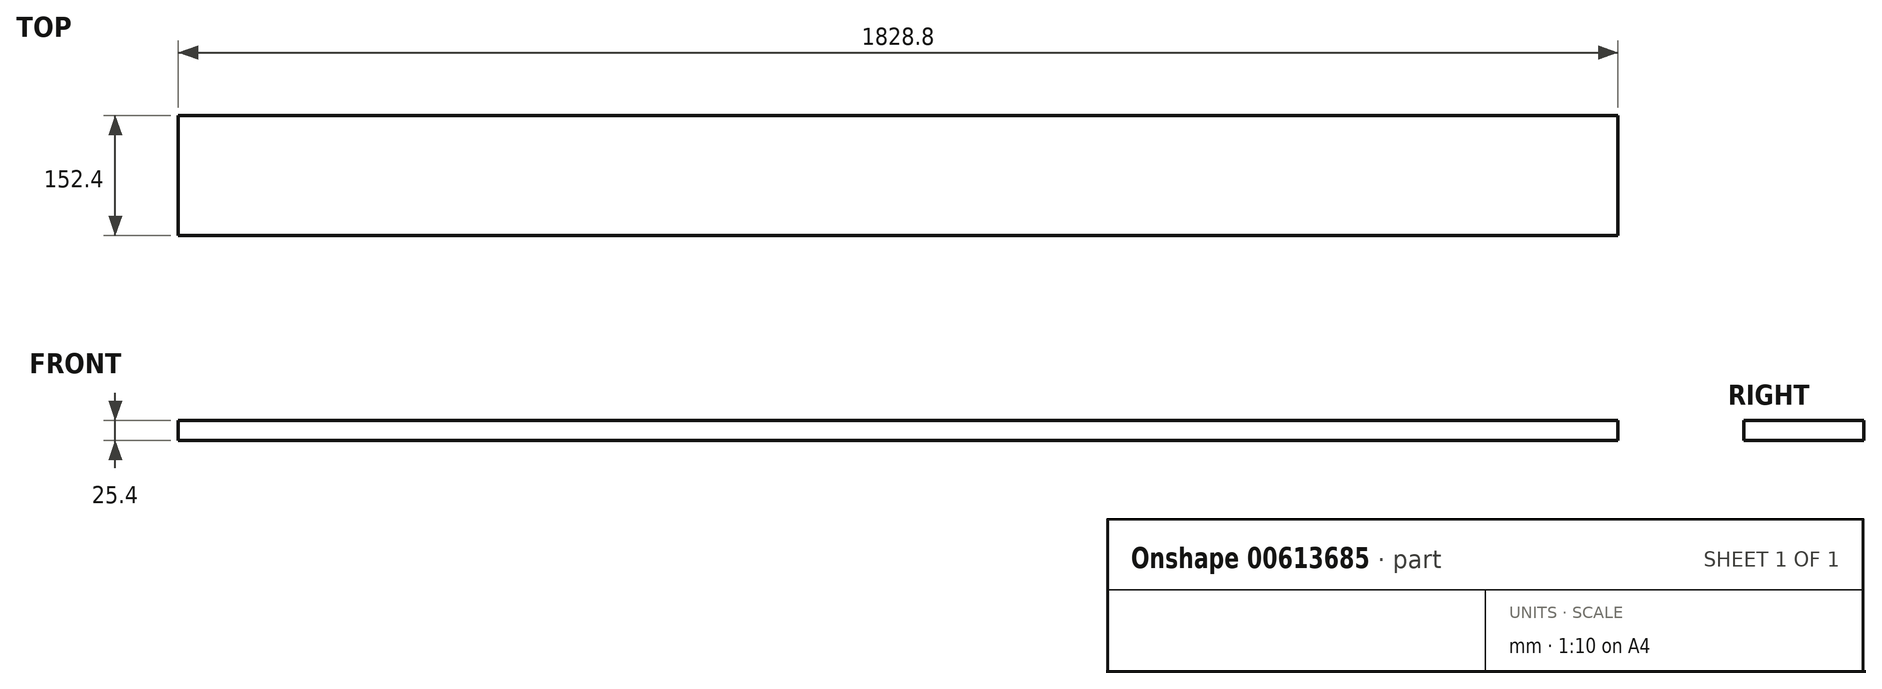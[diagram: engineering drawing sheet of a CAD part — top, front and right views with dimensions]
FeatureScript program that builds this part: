
annotation { "Feature Type Name" : "Feature", "Feature Type Description" : "" }
export const myFeature = defineFeature(function(context is Context, id is Id, definition is map)
    precondition{}
    {
        {
            var Q0;
            Q0=qCreatedBy(makeId("Top.planeOp"),FACE);
            var sketch = newSketch(context, id + "F0", { "sketchPlane" : qUnion([Q0])});
            skLineSegment(sketch, "E0.bottom", {"start": v(-916.5, 28.26) * mm, "end": v(912.3, 28.26) * mm});
            skLineSegment(sketch, "E0.top", {"start": v(-916.5, -124.14) * mm, "end": v(912.3, -124.14) * mm});
            skLineSegment(sketch, "E0.left", {"start": v(-916.5, 28.26) * mm, "end": v(-916.5, -124.14) * mm});
            skLineSegment(sketch, "E0.right", {"start": v(912.3, 28.26) * mm, "end": v(912.3, -124.14) * mm});
            skSolve(sketch);
        }
        {
            var Q0;
            Q0 = qSketchRegion(id + "F0", true);
            extrude(context, id + "F1", {"entities" : qUnion([Q0]), "depth" : 25.4 * mm, "offsetDistance" : 25.4 * mm});
        }
    });
